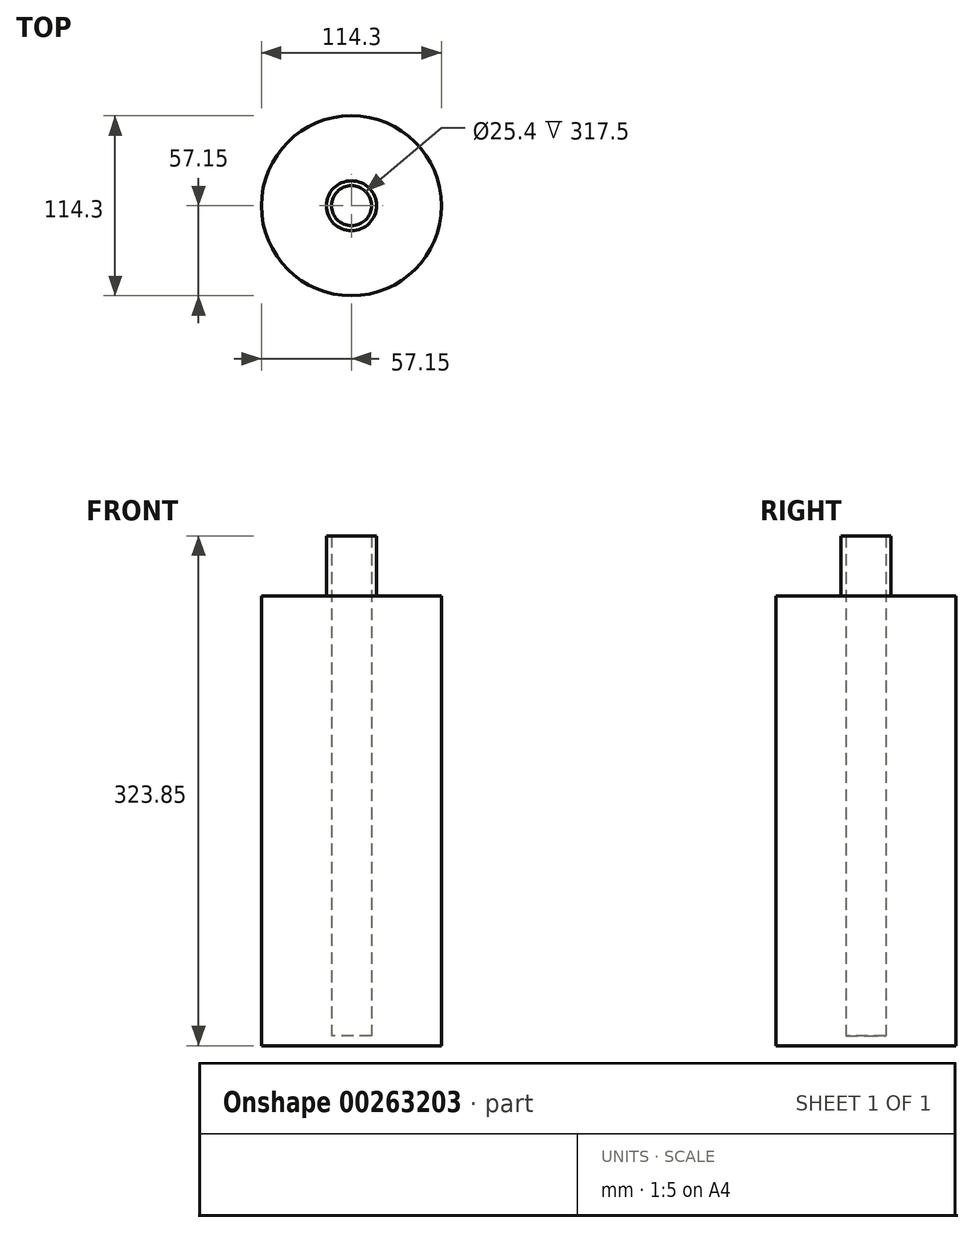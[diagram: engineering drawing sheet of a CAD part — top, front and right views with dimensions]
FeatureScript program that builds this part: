
annotation { "Feature Type Name" : "Feature", "Feature Type Description" : "" }
export const myFeature = defineFeature(function(context is Context, id is Id, definition is map)
    precondition{}
    {
        {
            var Q0;
            Q0=qCreatedBy(makeId("Top.planeOp"),FACE);
            var sketch = newSketch(context, id + "F0", { "sketchPlane" : qUnion([Q0])});
            skCircle(sketch, "E0", {"center": v(0, 0) * mm, "radius": 57.15 * mm});
            skCircle(sketch, "E1", {"center": v(0, 0) * mm, "radius": 12.7 * mm});
            skSolve(sketch);
        }
        {
            var Q0;
            Q0 = qSketchRegion(id + "F0", true);
            var Q1;
            Q1=makeQuery(id+"F0.imprint","IMPRINT",FACE,{"disambiguationData":[TD([[makeQuery(id+"F0.imprint","IMPRINT",EDGE,{"derivedFrom":sQuery(id+"F0.wireOp",EDGE,"E1")}),1.0]])]});
            extrude(context, id + "F1", {"entities" : qUnion([Q0, Q1]), "depth" : 6.35 * mm});
        }
        {
            var Q0;
            Q0=makeQuery(id+"F0.imprint","IMPRINT",FACE,{"disambiguationData":[TD([[makeQuery(id+"F0.imprint","IMPRINT",EDGE,{"derivedFrom":sQuery(id+"F0.wireOp",EDGE,"E0")}),1.0]])]});
            extrude(context, id + "F2", {"entities" : qUnion([Q0]), "operationType" : NewBodyOperationType.ADD, "depth" : 285.75 * mm});
        }
        {
            var Q0;
            Q0=makeQuery(id+"F2.opExtrude","CAP_FACE",FACE,{"disambiguationData":[OSD([sQuery(id+"F0.wireOp",EDGE,"E0"),sQuery(id+"F0.wireOp",EDGE,"E1")])],"isStart":false});
            var sketch = newSketch(context, id + "F3", { "sketchPlane" : qUnion([Q0])});
            skCircle(sketch, "E2", {"center": v(0, 0) * mm, "radius": 15.88 * mm});
            skSolve(sketch);
        }
        {
            var Q0;
            Q0=makeQuery(id+"F3.imprint","IMPRINT",FACE,{"disambiguationData":[TD([[makeQuery(id+"F3.imprint","IMPRINT",EDGE,{"derivedFrom":sQuery(id+"F3.wireOp",EDGE,"E2")}),1.0]])]});
            extrude(context, id + "F4", {"entities" : qUnion([Q0]), "operationType" : NewBodyOperationType.ADD, "depth" : 38.1 * mm});
        }
    });
